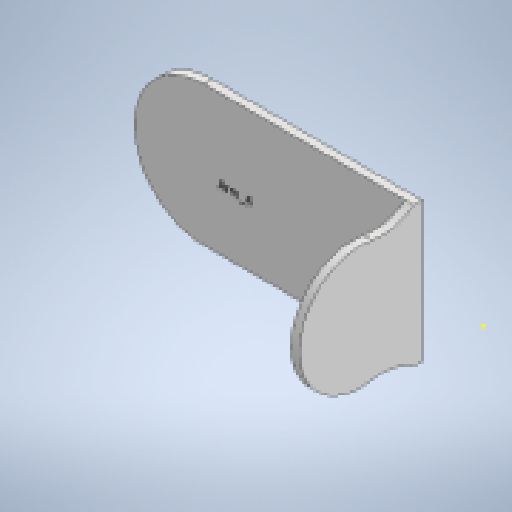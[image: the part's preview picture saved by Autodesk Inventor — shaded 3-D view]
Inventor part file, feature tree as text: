
AUTODESK INVENTOR PART (.ipt)
format: ipt  version: 2023 (Build 270158000, 158)  size: 148,992 bytes
history: native  units: mm
features: sketch x3, extrude x2, other x1, fillet x1
ambient origin geometry x8: Origin, YZ Plane, XZ Plane, XY Plane, X Axis, Y Axis, Z Axis, Center Point
bodies: Body1 (feature_tree)
feature tree (7):
  other  "實體1"
  extrude  "擠出1"  Depth=50.0mm
  extrude  "擠出2"  Depth=150.0mm
  fillet  "圓角1"  Radius=3.0mm
  sketch  "草圖3"
  sketch  "草圖1"
  sketch  "草圖2"
